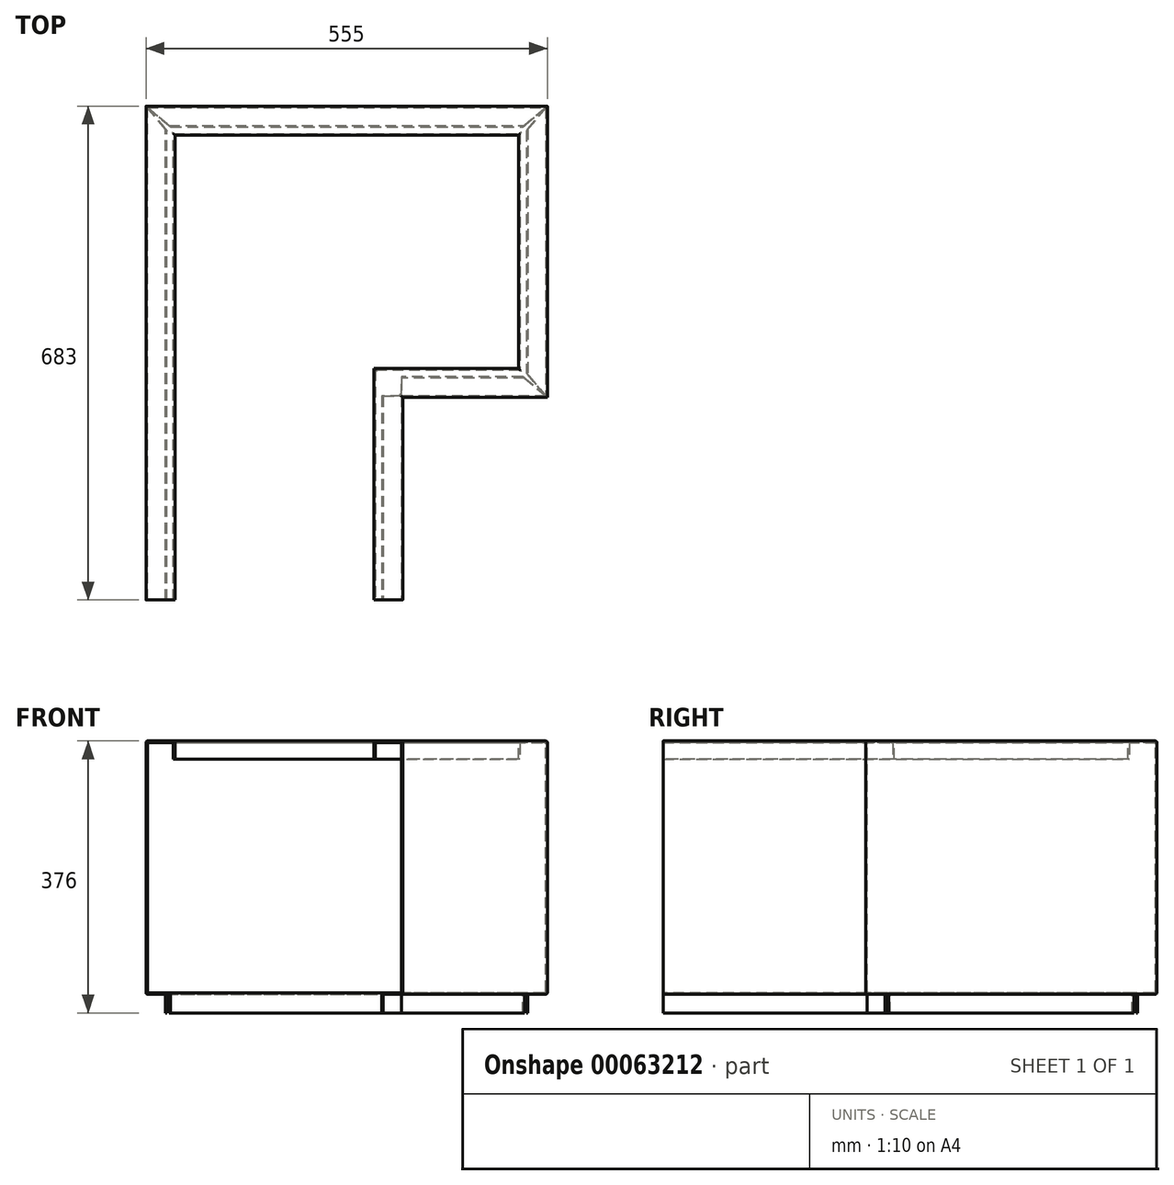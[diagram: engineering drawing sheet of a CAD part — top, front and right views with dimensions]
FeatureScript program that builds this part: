
annotation { "Feature Type Name" : "Feature", "Feature Type Description" : "" }
export const myFeature = defineFeature(function(context is Context, id is Id, definition is map)
    precondition{}
    {
        {
            var Q0;
            Q0=qCreatedBy(makeId("Front.planeOp"),FACE);
            var sketch = newSketch(context, id + "F0", { "sketchPlane" : qUnion([Q0])});
            skLineSegment(sketch, "E0", {"start": v(2, 0) * mm, "end": v(38, 0) * mm});
            skLineSegment(sketch, "E1", {"start": v(40, -2) * mm, "end": v(40, -25) * mm});
            skLineSegment(sketch, "E2", {"start": v(0, -2) * mm, "end": v(0, -348) * mm});
            skLineSegment(sketch, "E3", {"start": v(2, -350) * mm, "end": v(25, -350) * mm});
            skLineSegment(sketch, "E4", {"start": v(27, -352) * mm, "end": v(27, -376) * mm});
            skLineSegment(sketch, "E5.0", {"start": v(29, -350) * mm, "end": v(29, -376) * mm});
            skLineSegment(sketch, "E5.1", {"start": v(38, -4) * mm, "end": v(38, -25) * mm});
            skLineSegment(sketch, "E5.2", {"start": v(4, -2) * mm, "end": v(36, -2) * mm});
            skLineSegment(sketch, "E5.3", {"start": v(2, -4) * mm, "end": v(2, -346) * mm});
            skLineSegment(sketch, "E5.4", {"start": v(4, -348) * mm, "end": v(27, -348) * mm});
            skLineSegment(sketch, "E6", {"start": v(29, -376) * mm, "end": v(27, -376) * mm});
            skLineSegment(sketch, "E7", {"start": v(38, -25) * mm, "end": v(40, -25) * mm});
            skPoint(sketch, "E8.visualSharp", {"position": v(40, 0) * mm});
            skArc(sketch, "E8.filletArc", {"start": v(40, -2) * mm, "mid": v(39.41, -0.59) * mm, "end": v(38, 0) * mm});
            skArc(sketch, "E9.filletArc", {"start": v(38, -4) * mm, "mid": v(37.41, -2.59) * mm, "end": v(36, -2) * mm});
            skPoint(sketch, "E10.visualSharp", {"position": v(2, -2) * mm});
            skArc(sketch, "E10.filletArc", {"start": v(4, -2) * mm, "mid": v(2.59, -2.59) * mm, "end": v(2, -4) * mm});
            skPoint(sketch, "E11.visualSharp", {"position": v(0, 0) * mm});
            skArc(sketch, "E11.filletArc", {"start": v(2, 0) * mm, "mid": v(0.59, -0.59) * mm, "end": v(0, -2) * mm});
            skPoint(sketch, "E12.visualSharp", {"position": v(2, -348) * mm});
            skArc(sketch, "E12.filletArc", {"start": v(2, -346) * mm, "mid": v(2.59, -347.41) * mm, "end": v(4, -348) * mm});
            skPoint(sketch, "E13.visualSharp", {"position": v(0, -350) * mm});
            skArc(sketch, "E13.filletArc", {"start": v(0, -348) * mm, "mid": v(0.59, -349.41) * mm, "end": v(2, -350) * mm});
            skPoint(sketch, "E14.visualSharp", {"position": v(27, -350) * mm});
            skArc(sketch, "E14.filletArc", {"start": v(27, -352) * mm, "mid": v(26.41, -350.59) * mm, "end": v(25, -350) * mm});
            skPoint(sketch, "E15.visualSharp", {"position": v(29, -348) * mm});
            skArc(sketch, "E15.filletArc", {"start": v(29, -350) * mm, "mid": v(28.41, -348.59) * mm, "end": v(27, -348) * mm});
            skSolve(sketch);
        }
        {
            var Q0;
            Q0=qCreatedBy(makeId("Top.planeOp"),FACE);
            var sketch = newSketch(context, id + "F1", { "sketchPlane" : qUnion([Q0])});
            skLineSegment(sketch, "E16", {"start": v(0, 0) * mm, "end": v(0, 683) * mm});
            skLineSegment(sketch, "E17", {"start": v(0, 683) * mm, "end": v(555, 683) * mm});
            skLineSegment(sketch, "E18", {"start": v(555, 683) * mm, "end": v(555, 280) * mm});
            skLineSegment(sketch, "E19", {"start": v(555, 280) * mm, "end": v(355, 280) * mm});
            skLineSegment(sketch, "E20", {"start": v(355, 280) * mm, "end": v(355, 0) * mm});
            skSolve(sketch);
        }
        {
            var Q0;
            Q0=makeQuery(id+"F0.imprint","IMPRINT",FACE,{"disambiguationData":[TD([[makeQuery(id+"F0.imprint","IMPRINT",EDGE,{"derivedFrom":sQuery(id+"F0.wireOp",EDGE,"E0")}),-1.0]])]});
            var Q1;
            Q1=sQuery(id+"F1.wireOp",EDGE,"E16");
            var Q2;
            Q2=sQuery(id+"F1.wireOp",EDGE,"E17");
            var Q3;
            Q3=sQuery(id+"F1.wireOp",EDGE,"E18");
            var Q4;
            Q4=sQuery(id+"F1.wireOp",EDGE,"E19");
            var Q5;
            Q5=sQuery(id+"F1.wireOp",EDGE,"E20");
            sweep(context, id + "F2", {"profiles" : qUnion([Q0]), "path" : qUnion([Q1, Q2, Q3, Q4, Q5])});
        }
        {
            var Q0;
            Q0=makeQuery(id+"F2.opSweep","SWEPT_FACE",FACE,{"disambiguationData":[OSD([sQuery(id+"F0.wireOp",EDGE,"E5.4"),sQuery(id+"F1.wireOp",EDGE,"E16")])]});
            var sketch = newSketch(context, id + "F3", { "sketchPlane" : qUnion([Q0])});
            skLineSegment(sketch, "E21", {"start": v(29, 648.82) * mm, "end": v(2, 681) * mm});
            skLineSegment(sketch, "E22", {"start": v(2, 681) * mm, "end": v(34.18, 654) * mm});
            skLineSegment(sketch, "E23", {"start": v(34.18, 654) * mm, "end": v(29, 654) * mm});
            skLineSegment(sketch, "E24", {"start": v(29, 654) * mm, "end": v(29, 648.82) * mm});
            skLineSegment(sketch, "E25", {"start": v(553, 681) * mm, "end": v(520.82, 654) * mm});
            skLineSegment(sketch, "E26", {"start": v(520.82, 654) * mm, "end": v(526, 654) * mm});
            skLineSegment(sketch, "E27", {"start": v(526, 654) * mm, "end": v(526, 648.82) * mm});
            skLineSegment(sketch, "E28", {"start": v(526, 648.82) * mm, "end": v(553, 681) * mm});
            skLineSegment(sketch, "E29", {"start": v(553, 282) * mm, "end": v(526, 314.18) * mm});
            skLineSegment(sketch, "E30", {"start": v(526, 314.18) * mm, "end": v(526, 309) * mm});
            skLineSegment(sketch, "E31", {"start": v(526, 309) * mm, "end": v(520.82, 309) * mm});
            skLineSegment(sketch, "E32", {"start": v(520.82, 309) * mm, "end": v(553, 282) * mm});
            skLineSegment(sketch, "E33", {"start": v(353, 282) * mm, "end": v(353, 309) * mm});
            skLineSegment(sketch, "E34", {"start": v(353, 309) * mm, "end": v(326, 309) * mm});
            skLineSegment(sketch, "E35", {"start": v(326, 309) * mm, "end": v(326, 282) * mm});
            skLineSegment(sketch, "E36", {"start": v(326, 282) * mm, "end": v(353, 282) * mm});
            skSolve(sketch);
        }
        {
            var Q0;
            Q0=qSketchRegion(id+"F3",true);
            extrude(context, id + "F4", {"entities" : qUnion([Q0]), "operationType" : NewBodyOperationType.REMOVE, "oppositeDirection" : true, "depth" : 40 * mm});
        }
    });
